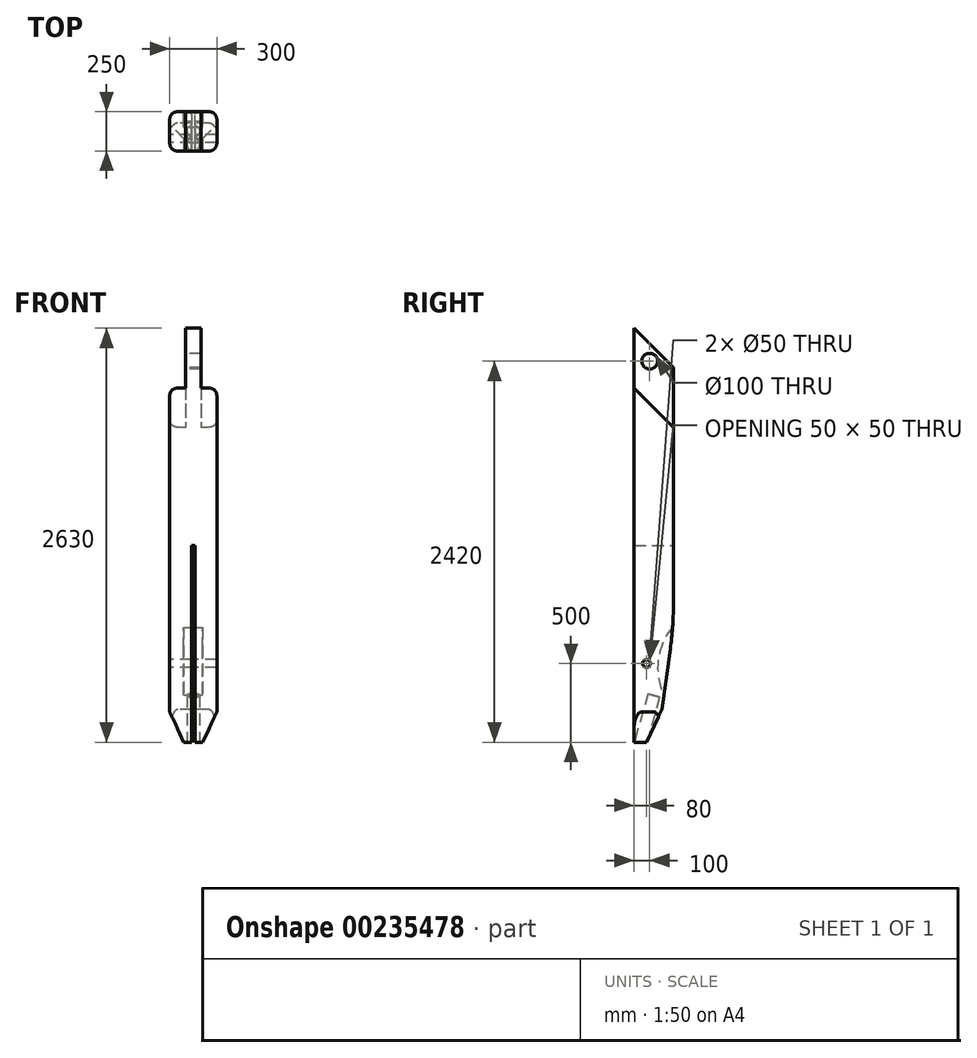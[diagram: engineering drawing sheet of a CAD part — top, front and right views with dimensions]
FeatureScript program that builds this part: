
annotation { "Feature Type Name" : "Feature", "Feature Type Description" : "" }
export const myFeature = defineFeature(function(context is Context, id is Id, definition is map)
    precondition{}
    {
        {
            var Q0;
            Q0=qCreatedBy(makeId("Right.planeOp"),FACE);
            var sketch = newSketch(context, id + "F0", { "sketchPlane" : qUnion([Q0])});
            skLineSegment(sketch, "E0", {"start": v(0, 0) * mm, "end": v(0, 2630) * mm});
            skLineSegment(sketch, "E1", {"start": v(0, 2630) * mm, "end": v(250, 2380) * mm});
            skLineSegment(sketch, "E2", {"start": v(250, 2380) * mm, "end": v(250, 870) * mm});
            skLineSegment(sketch, "E3", {"start": v(0, 2250) * mm, "end": v(250, 2000) * mm});
            skLineSegment(sketch, "E4", {"start": v(0, 0) * mm, "end": v(80, 0) * mm});
            skLineSegment(sketch, "E5", {"start": v(80, 0) * mm, "end": v(176.46, 206.85) * mm});
            skLineSegment(sketch, "E6", {"start": v(176.46, 206.85) * mm, "end": v(230.54, 591.65) * mm});
            skArc(sketch, "E7", {"start": v(250, 870) * mm, "mid": v(245.13, 730.49) * mm, "end": v(230.54, 591.65) * mm});
            skSolve(sketch);
        }
        {
            var Q0;
            {var subQ1=sQuery(id+"F0.wireOp",EDGE,"E3");Q0=makeQuery(id+"F0.imprint","IMPRINT",FACE,{"disambiguationData":[TD([[makeQuery(id+"F0.imprint","IMPRINT",EDGE,{"derivedFrom":subQ1}),-1.0]])]});}
            extrude(context, id + "F1", {"entities" : qUnion([Q0]), "endBound" : BoundingType.SYMMETRIC, "depth" : 300 * mm});
        }
        {
            var Q0;
            {var subQ0=sQuery(id+"F0.wireOp",EDGE,"E1");Q0=makeQuery(id+"F0.imprint","IMPRINT",FACE,{"disambiguationData":[TD([[makeQuery(id+"F0.imprint","IMPRINT",EDGE,{"derivedFrom":subQ0}),-1.0]])]});}
            extrude(context, id + "F2", {"entities" : qUnion([Q0]), "operationType" : NewBodyOperationType.ADD, "endBound" : BoundingType.SYMMETRIC, "depth" : 100 * mm});
        }
        {
            var Q0;
            {var subQ0=sQuery(id+"F0.wireOp",EDGE,"E2");Q0=makeQuery(id+"F2.boolean.opBoolean","MERGE",FACE,{"derivedFrom":[makeQuery(id+"F1.opExtrude","SWEPT_FACE",FACE,{"disambiguationData":[OSD([subQ0])]}),makeQuery(id+"F2.opExtrude","SWEPT_FACE",FACE,{"disambiguationData":[OSD([subQ0])]})]});}
            var sketch = newSketch(context, id + "F3", { "sketchPlane" : qUnion([Q0])});
            skLineSegment(sketch, "E8", {"start": v(-10, 0) * mm, "end": v(-10, 1250) * mm});
            skLineSegment(sketch, "E9", {"start": v(-10, 1250) * mm, "end": v(10, 1250) * mm});
            skLineSegment(sketch, "E10", {"start": v(10, 1250) * mm, "end": v(10, 0) * mm});
            skLineSegment(sketch, "E11", {"start": v(10, 0) * mm, "end": v(-10, 0) * mm});
            skSolve(sketch);
        }
        {
            var Q0;
            Q0 = qSketchRegion(id + "F3", true);
            extrude(context, id + "F4", {"entities" : qUnion([Q0]), "operationType" : NewBodyOperationType.REMOVE, "oppositeDirection" : true, "depth" : 307 * mm});
        }
        {
            var Q0;
            Q0=makeQuery(id+"F1.opExtrude","CAP_FACE",FACE,{"disambiguationData":[OSD([sQuery(id+"F0.wireOp",EDGE,"E0"),sQuery(id+"F0.wireOp",EDGE,"E2"),sQuery(id+"F0.wireOp",EDGE,"E3"),sQuery(id+"F0.wireOp",EDGE,"LOpwU0jk-QSrG-zGIa-wXVH-NvAEkFoPySG0"),sQuery(id+"F0.wireOp",EDGE,"E4")])],"isStart":true});
            var sketch = newSketch(context, id + "F5", { "sketchPlane" : qUnion([Q0])});
            skCircle(sketch, "E12", {"center": v(-80, 500) * mm, "radius": 25 * mm});
            skSolve(sketch);
        }
        {
            var Q0;
            Q0 = qSketchRegion(id + "F5", true);
            extrude(context, id + "F6", {"entities" : qUnion([Q0]), "operationType" : NewBodyOperationType.REMOVE, "endBound" : BoundingType.THROUGH_ALL, "oppositeDirection" : true, "depth" : 25 * mm});
        }
        {
            var Q0;
            Q0=makeQuery(id+"F2.opExtrude","CAP_FACE",FACE,{"disambiguationData":[OSD([sQuery(id+"F0.wireOp",EDGE,"E0"),sQuery(id+"F0.wireOp",EDGE,"E1"),sQuery(id+"F0.wireOp",EDGE,"E2"),sQuery(id+"F0.wireOp",EDGE,"E3")])],"isStart":true});
            var sketch = newSketch(context, id + "F7", { "sketchPlane" : qUnion([Q0])});
            skCircle(sketch, "E13", {"center": v(-100, 2420) * mm, "radius": 50 * mm});
            skSolve(sketch);
        }
        {
            var Q0;
            Q0 = qSketchRegion(id + "F7", true);
            extrude(context, id + "F8", {"entities" : qUnion([Q0]), "operationType" : NewBodyOperationType.REMOVE, "endBound" : BoundingType.UP_TO_NEXT, "oppositeDirection" : true, "depth" : 25 * mm});
        }
        {
            var Q0;
            {var subQ0=sQuery(id+"F0.wireOp",EDGE,"E0");Q0=makeQuery(id+"F2.boolean.opBoolean","MERGE",FACE,{"derivedFrom":[makeQuery(id+"F1.opExtrude","SWEPT_FACE",FACE,{"disambiguationData":[OSD([subQ0])]}),makeQuery(id+"F2.opExtrude","SWEPT_FACE",FACE,{"disambiguationData":[OSD([subQ0])]})]});}
            var sketch = newSketch(context, id + "F9", { "sketchPlane" : qUnion([Q0])});
            skLineSegment(sketch, "E14", {"start": v(60, 0) * mm, "end": v(150, 193) * mm});
            skLineSegment(sketch, "E15", {"start": v(150, 193) * mm, "end": v(150, 0) * mm});
            skLineSegment(sketch, "E16", {"start": v(150, 0) * mm, "end": v(60, 0) * mm});
            skLineSegment(sketch, "E17.MirrorCS", {"start": v(-60, 0) * mm, "end": v(-150, 193) * mm});
            skLineSegment(sketch, "E18.MirrorCS", {"start": v(-150, 0) * mm, "end": v(-60, 0) * mm});
            skLineSegment(sketch, "E19.MirrorCS", {"start": v(-150, 193) * mm, "end": v(-150, 0) * mm});
            skSolve(sketch);
        }
        {
            var Q0;
            Q0 = qSketchRegion(id + "F9", true);
            extrude(context, id + "F10", {"entities" : qUnion([Q0]), "operationType" : NewBodyOperationType.REMOVE, "oppositeDirection" : true, "depth" : 223 * mm});
        }
        {
            var Q0;
            Q0=qCreatedBy(makeId("Right.planeOp"),FACE);
            var sketch = newSketch(context, id + "F11", { "sketchPlane" : qUnion([Q0])});
            skLineSegment(sketch, "E20.0", {"start": v(176.46, 206.85) * mm, "end": v(230.54, 591.65) * mm});
            skPoint(sketch, "E21.0", {"position": v(245.13, 730.49) * mm});
            skPoint(sketch, "E22", {"position": v(189.55, 300) * mm});
            skArc(sketch, "E23", {"start": v(245.13, 730.49) * mm, "mid": v(153.87, 523.44) * mm, "end": v(189.55, 300) * mm});
            skArc(sketch, "E24.0", {"start": v(250, 870) * mm, "mid": v(245.13, 730.49) * mm, "end": v(230.54, 591.65) * mm});
            skLineSegment(sketch, "E25", {"start": v(245.13, 730.49) * mm, "end": v(230.54, 591.65) * mm});
            skLineSegment(sketch, "E26", {"start": v(245.13, 730.49) * mm, "end": v(321.97, 722.41) * mm});
            skLineSegment(sketch, "E27", {"start": v(321.97, 722.41) * mm, "end": v(299.65, 510.04) * mm});
            skLineSegment(sketch, "E28", {"start": v(299.65, 510.04) * mm, "end": v(265.2, 409.19) * mm});
            skLineSegment(sketch, "E29", {"start": v(265.2, 409.19) * mm, "end": v(265.2, 311.27) * mm});
            skLineSegment(sketch, "E30", {"start": v(265.2, 311.27) * mm, "end": v(189.55, 300) * mm});
            skSolve(sketch);
        }
        {
            var Q0;
            Q0 = qSketchRegion(id + "F11", true);
            extrude(context, id + "F12", {"entities" : qUnion([Q0]), "operationType" : NewBodyOperationType.REMOVE, "endBound" : BoundingType.SYMMETRIC, "oppositeDirection" : true, "depth" : 120 * mm});
        }
        {
            var Q0;
            Q0=qCreatedBy(makeId("Right.planeOp"),FACE);
            var sketch = newSketch(context, id + "F13", { "sketchPlane" : qUnion([Q0])});
            skArc(sketch, "E31.0", {"start": v(245.13, 730.49) * mm, "mid": v(153.87, 523.44) * mm, "end": v(189.55, 300) * mm, "construction": true});
            skLineSegment(sketch, "E32", {"start": v(0, 0) * mm, "end": v(165.9, 581.9) * mm});
            skLineSegment(sketch, "E33", {"start": v(0, 0) * mm, "end": v(365.8, -104.3) * mm, "construction": true});
            skSolve(sketch);
        }
        {
            var Q0;
            Q0=sQuery(id+"F13.wireOp",EDGE,"E33");
            var Q1;
            {var subQ0=sQuery(id+"F0.wireOp",EDGE,"E0");Q1=makeQuery(id+"F4.boolean.opBoolean","INTERSECT",EDGE,{"derivedFrom":[makeQuery(id+"F2.boolean.opBoolean","MERGE",FACE,{"derivedFrom":[makeQuery(id+"F1.opExtrude","SWEPT_FACE",FACE,{"disambiguationData":[OSD([subQ0])]}),makeQuery(id+"F2.opExtrude","SWEPT_FACE",FACE,{"disambiguationData":[OSD([subQ0])]})]}),makeQuery(id+"F4.opExtrude","SWEPT_FACE",FACE,{"disambiguationData":[OSD([sQuery(id+"F3.wireOp",EDGE,"E10")])]})]});}
            cPlane(context, id + "F14", {"entities" : qUnion([Q0, Q1]), "cplaneType" : CPlaneType.LINE_ANGLE, "offset" : 25 * mm, "angle" : 90 * degree, "width" : 150 * mm, "height" : 150 * mm});
        }
        {
            var Q0;
            Q0=qCreatedBy(id+"F14.planeOp",FACE);
            var sketch = newSketch(context, id + "F15", { "sketchPlane" : qUnion([Q0])});
            skCircle(sketch, "E34", {"center": v(0, -40) * mm, "radius": 40 * mm});
            skSolve(sketch);
        }
        {
            var Q0;
            Q0 = qSketchRegion(id + "F15", true);
            extrude(context, id + "F16", {"entities" : qUnion([Q0]), "operationType" : NewBodyOperationType.REMOVE, "oppositeDirection" : true, "depth" : 320 * mm});
        }
        {
            var Q0;
            Q0=makeQuery(id+"F1.opExtrude","CAP_EDGE",EDGE,{"disambiguationData":[OSD([sQuery(id+"F0.wireOp",EDGE,"E2")])],"isStart":true});
            var Q1;
            Q1=makeQuery(id+"F1.opExtrude","CAP_EDGE",EDGE,{"disambiguationData":[OSD([sQuery(id+"F0.wireOp",EDGE,"E2")])],"isStart":false});
            var Q2;
            Q2=makeQuery(id+"F1.opExtrude","CAP_EDGE",EDGE,{"disambiguationData":[OSD([sQuery(id+"F0.wireOp",EDGE,"E7")])],"isStart":true});
            var Q3;
            Q3=makeQuery(id+"F1.opExtrude","CAP_EDGE",EDGE,{"disambiguationData":[OSD([sQuery(id+"F0.wireOp",EDGE,"E6")])],"isStart":true});
            var Q4;
            Q4=makeQuery(id+"F1.opExtrude","CAP_EDGE",EDGE,{"disambiguationData":[OSD([sQuery(id+"F0.wireOp",EDGE,"E6")])],"isStart":false});
            var Q5;
            Q5=makeQuery(id+"F1.opExtrude","CAP_EDGE",EDGE,{"disambiguationData":[OSD([sQuery(id+"F0.wireOp",EDGE,"E7")])],"isStart":false});
            var Q6;
            Q6=makeQuery(id+"F1.opExtrude","CAP_EDGE",EDGE,{"disambiguationData":[OSD([sQuery(id+"F0.wireOp",EDGE,"E0")])],"isStart":true});
            var Q7;
            Q7=makeQuery(id+"F1.opExtrude","CAP_EDGE",EDGE,{"disambiguationData":[OSD([sQuery(id+"F0.wireOp",EDGE,"E0")])],"isStart":false});
            fillet(context, id + "F17", {"entities" : qUnion([Q0, Q1, Q2, Q3, Q4, Q5, Q6, Q7]), "radius" : 50 * mm, "allowEdgeOverflow" : false});
        }
    });
